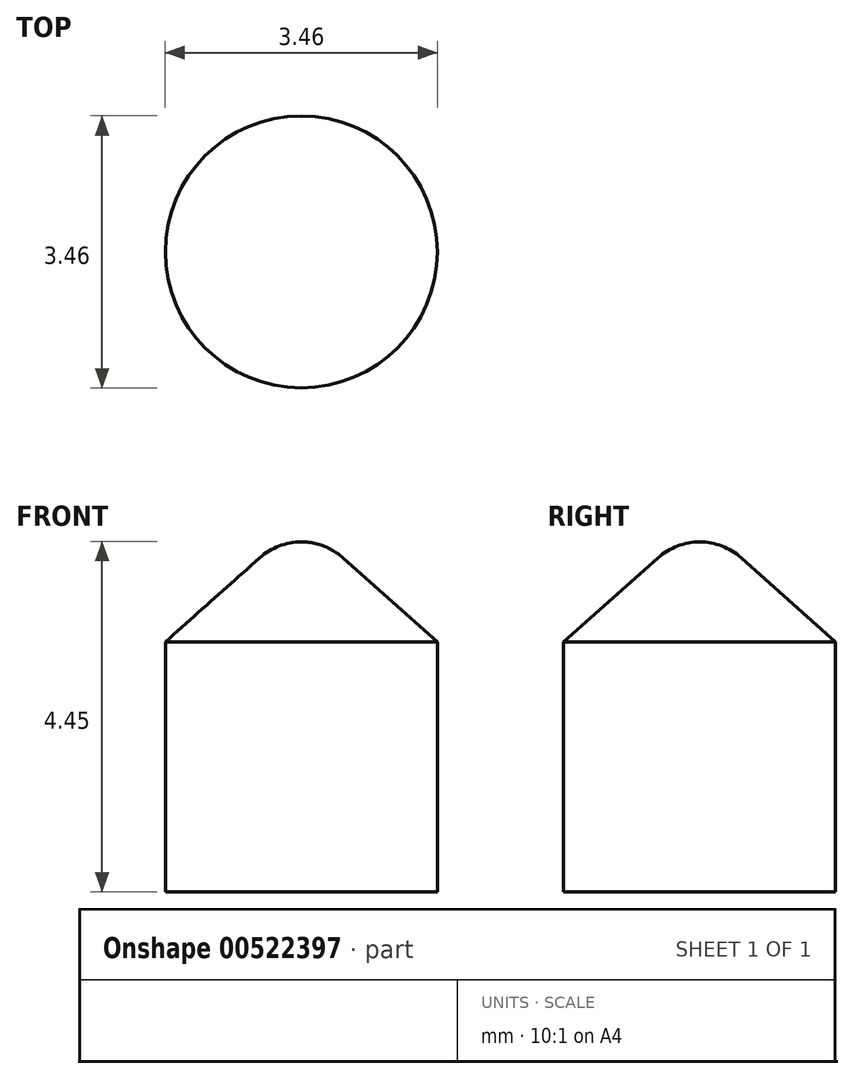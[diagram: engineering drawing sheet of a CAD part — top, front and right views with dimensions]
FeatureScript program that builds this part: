
annotation { "Feature Type Name" : "Feature", "Feature Type Description" : "" }
export const myFeature = defineFeature(function(context is Context, id is Id, definition is map)
    precondition{}
    {
        {
            var Q0;
            Q0=qCreatedBy(makeId("Front.planeOp"),FACE);
            var sketch = newSketch(context, id + "F0", { "sketchPlane" : qUnion([Q0])});
            skLineSegment(sketch, "E0", {"start": v(0, 0) * mm, "end": v(1.73, 0) * mm});
            skLineSegment(sketch, "E1", {"start": v(1.73, 0) * mm, "end": v(1.73, 3.18) * mm});
            skLineSegment(sketch, "E2", {"start": v(1.73, 3.18) * mm, "end": v(0.53, 4.24) * mm});
            skLineSegment(sketch, "E3", {"start": v(0, 4.45) * mm, "end": v(0, 0) * mm});
            skArc(sketch, "E4", {"start": v(0, 4.45) * mm, "mid": v(0.28, 4.4) * mm, "end": v(0.53, 4.24) * mm});
            skSolve(sketch);
        }
        {
            var Q0;
            Q0 = qSketchRegion(id + "F0", true);
            var Q1;
            Q1=sQuery(id+"F0.wireOp",EDGE,"E3");
            revolve(context, id + "F1", {"entities" : qUnion([Q0]), "axis" : qUnion([Q1]), "revolveType" : RevolveType.FULL, "oppositeDirection" : true});
        }
    });
